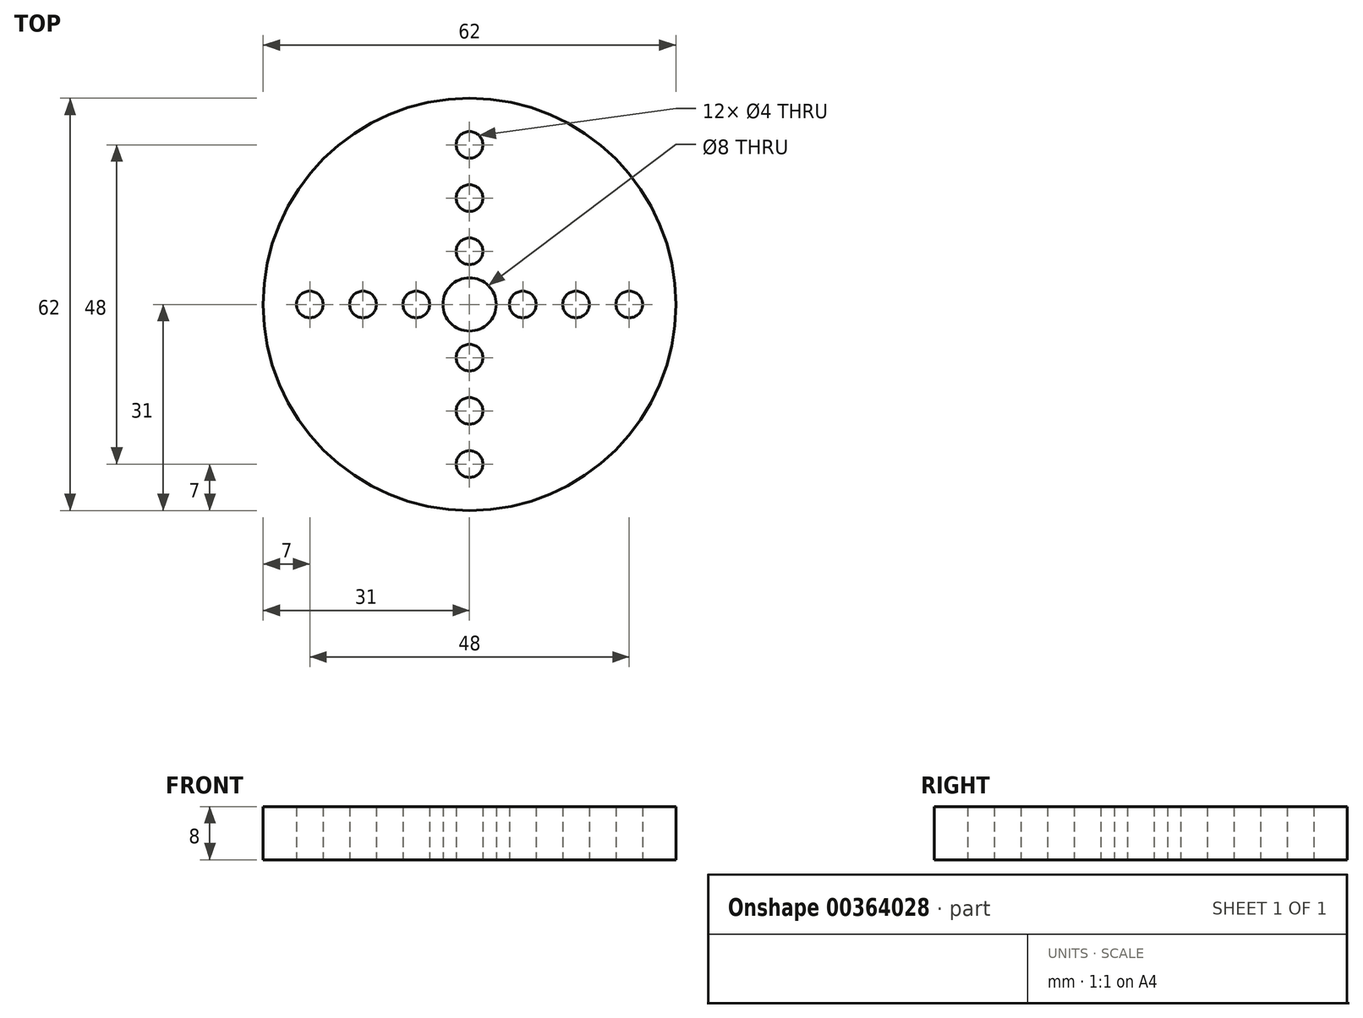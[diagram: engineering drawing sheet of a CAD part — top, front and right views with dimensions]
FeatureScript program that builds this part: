
annotation { "Feature Type Name" : "Feature", "Feature Type Description" : "" }
export const myFeature = defineFeature(function(context is Context, id is Id, definition is map)
    precondition{}
    {
        {
            var Q0;
            Q0=qCreatedBy(makeId("Top.planeOp"),FACE);
            var sketch = newSketch(context, id + "F0", { "sketchPlane" : qUnion([Q0])});
            skCircle(sketch, "E0", {"center": v(0, 0) * mm, "radius": 31 * mm});
            skCircle(sketch, "E1", {"center": v(0, 0) * mm, "radius": 4 * mm});
            skLineSegment(sketch, "E2", {"start": v(0, 0) * mm, "end": v(-8, 0) * mm, "construction": true});
            skLineSegment(sketch, "E3", {"start": v(-8, 0) * mm, "end": v(-16, 0) * mm, "construction": true});
            skCircle(sketch, "E4", {"center": v(-8, 0) * mm, "radius": 2 * mm});
            skCircle(sketch, "E5", {"center": v(-16, 0) * mm, "radius": 2 * mm});
            skLineSegment(sketch, "E6.anchor1", {"start": v(0, 0) * mm, "end": v(-16, 0) * mm, "construction": true});
            skLineSegment(sketch, "E6.anchor2", {"start": v(0, 0) * mm, "end": v(0, -16) * mm, "construction": true});
            skLineSegment(sketch, "E7", {"start": v(-16, 0) * mm, "end": v(-24, 0) * mm, "construction": true});
            skCircle(sketch, "E8", {"center": v(-24, 0) * mm, "radius": 2 * mm});
            skCircle(sketch, "E9.1.0", {"center": v(0, -8) * mm, "radius": 2 * mm});
            skCircle(sketch, "E9.1.1", {"center": v(0, -16) * mm, "radius": 2 * mm});
            skCircle(sketch, "E9.1.2", {"center": v(0, -24) * mm, "radius": 2 * mm});
            skCircle(sketch, "E9.2.0", {"center": v(8, 0) * mm, "radius": 2 * mm});
            skCircle(sketch, "E9.2.1", {"center": v(16, 0) * mm, "radius": 2 * mm});
            skCircle(sketch, "E9.2.2", {"center": v(24, 0) * mm, "radius": 2 * mm});
            skCircle(sketch, "E9.3.0", {"center": v(0, 8) * mm, "radius": 2 * mm});
            skCircle(sketch, "E9.3.1", {"center": v(0, 16) * mm, "radius": 2 * mm});
            skCircle(sketch, "E9.3.2", {"center": v(0, 24) * mm, "radius": 2 * mm});
            skSolve(sketch);
        }
        {
            var Q0;
            Q0 = qSketchRegion(id + "F0", true);
            extrude(context, id + "F1", {"entities" : qUnion([Q0]), "depth" : 8 * mm});
        }
    });
